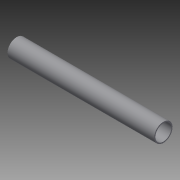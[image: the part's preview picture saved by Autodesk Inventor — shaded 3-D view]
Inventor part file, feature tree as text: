
AUTODESK INVENTOR PART (.ipt)
format: ipt  version: 2014 (Build 180170000, 170)  size: 85,504 bytes
history: native  units: in
note: dims shown in document units (in); Inventor stores cm internally (conversion verified against a paired STEP export)
features: extrude x1, sketch x1
ambient origin geometry x8: Origin, YZ Plane, XZ Plane, XY Plane, X Axis, Y Axis, Z Axis, Center Point
bodies: Solid1 (feature_tree)
feature tree (2):
  extrude  "Extrusion1"  Depth=5.25in
  sketch  "Sketch1"  dims[d0=0.5in d1=0.4375in d2=5.25in d3=0.0in]
